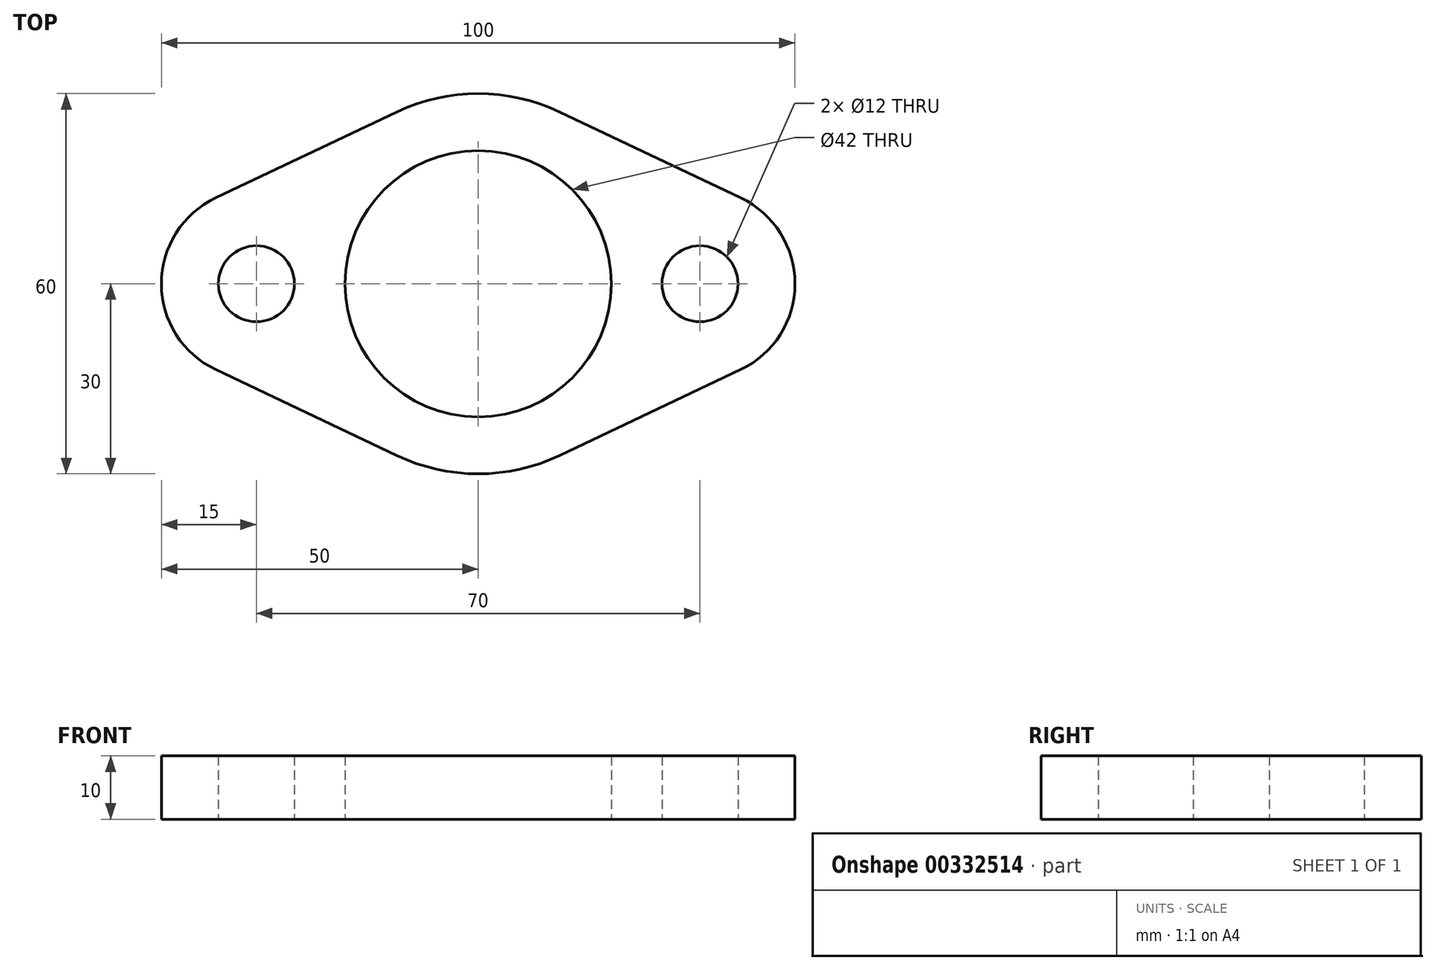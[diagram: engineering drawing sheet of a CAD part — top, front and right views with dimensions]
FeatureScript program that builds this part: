
annotation { "Feature Type Name" : "Feature", "Feature Type Description" : "" }
export const myFeature = defineFeature(function(context is Context, id is Id, definition is map)
    precondition{}
    {
        {
            var Q0;
            Q0=qCreatedBy(makeId("Top.planeOp"),FACE);
            var sketch = newSketch(context, id + "F0", { "sketchPlane" : qUnion([Q0])});
            skCircle(sketch, "E0", {"center": v(0, 0) * mm, "radius": 21 * mm});
            skArc(sketch, "E1", {"start": v(-12.86, -27.1) * mm, "mid": v(0, -30) * mm, "end": v(12.86, -27.1) * mm});
            skPoint(sketch, "E2", {"position": v(35, 0) * mm});
            skPoint(sketch, "E3", {"position": v(-35, 0) * mm});
            skCircle(sketch, "E4", {"center": v(35, 0) * mm, "radius": 6 * mm});
            skArc(sketch, "E5", {"start": v(41.43, -13.55) * mm, "mid": v(50, 0) * mm, "end": v(41.43, 13.55) * mm});
            skCircle(sketch, "E6", {"center": v(-35, 0) * mm, "radius": 6 * mm});
            skArc(sketch, "E7", {"start": v(-41.43, 13.55) * mm, "mid": v(-50, 0) * mm, "end": v(-41.43, -13.55) * mm});
            skLineSegment(sketch, "E8", {"start": v(-41.43, 13.55) * mm, "end": v(-12.86, 27.1) * mm});
            skLineSegment(sketch, "E9", {"start": v(12.86, 27.1) * mm, "end": v(41.43, 13.55) * mm});
            skLineSegment(sketch, "E10", {"start": v(12.86, -27.1) * mm, "end": v(41.43, -13.55) * mm});
            skLineSegment(sketch, "E11", {"start": v(-41.43, -13.55) * mm, "end": v(-12.86, -27.1) * mm});
            skArc(sketch, "E12.trimOffspring", {"start": v(12.86, 27.1) * mm, "mid": v(0, 30) * mm, "end": v(-12.86, 27.1) * mm});
            skSolve(sketch);
        }
        {
            var Q0;
            Q0=makeQuery(id+"F0.imprint","IMPRINT",FACE,{"disambiguationData":[TD([[makeQuery(id+"F0.imprint","IMPRINT",EDGE,{"derivedFrom":sQuery(id+"F0.wireOp",EDGE,"E0")}),-1.0]])]});
            extrude(context, id + "F1", {"entities" : qUnion([Q0]), "depth" : 10 * mm});
        }
    });
